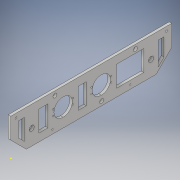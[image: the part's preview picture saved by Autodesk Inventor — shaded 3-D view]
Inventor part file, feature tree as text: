
AUTODESK INVENTOR PART (.ipt)
format: ipt  version: 2017 (Build 210142000, 142)  size: 301,568 bytes
history: native  units: in
note: dims shown in document units (in); Inventor stores cm internally (conversion verified against a paired STEP export)
features: sketch x15, hole x8, extrude x7, chamfer x3, thicken_offset x1, projected_geometry x1
ambient origin geometry x8: Origin, YZ Plane, XZ Plane, XY Plane, X Axis, Y Axis, Z Axis, Center Point
bodies: Solid1 (feature_tree)
feature tree (35):
  extrude  "Extrusion1"  Depth=15.5in
  sketch  "Sketch3"  dims[d4=2.0in]
  sketch  "Sketch4"  dims[d5=1.0in]
  chamfer  "Chamfer1"  Distance=0.25in
  chamfer  "Chamfer2"  Distance=1.5in Angle=45.0deg
  hole  "Hole1"  [1 undecoded]
  hole  "Hole3"  [1 undecoded]
  sketch  "Sketch8"  dims[d13=1.5in d14=0.125in d15=45.0deg d16=2.0in]
  hole  "Hole4"  [1 undecoded]
  hole  "Hole6"  [1 undecoded]
  extrude  "Extrusion2"  Depth=0.5in
  thicken_offset  "Thicken1"
  sketch  "Sketch16"  dims[d20=0.501in d21=0.75in d22=0.375in d23=0.25in d24=0.5635in d25=1.0in d26=0.8108in d42=0.394in]
  sketch  "Sketch17"  dims[d43=3.75in d44=3.75in]
  sketch  "Sketch18"  dims[d45=0.144in d46=0.5in]
  hole  "Hole10"  [1 undecoded]
  hole  "Hole11"  [1 undecoded]
  hole  "Hole12"  [1 undecoded]
  hole  "Hole13"  [1 undecoded]
  sketch  "Sketch19"  dims[d47=0.5in]
  sketch  "Sketch20"  dims[d48=0.188in d49=0.75in d50=0.375in d51=0.25in d52=0.5635in d53=1.0in d54=0.8108in d57=0.394in]
  extrude  "Extrusion3"  Depth=0.75in
  extrude  "Extrusion4"  Depth=0.75in
  sketch  "Sketch21"  dims[d61=0.14in d62=0.75in d63=0.375in d64=0.25in d65=0.5635in d66=1.0in d67=0.8108in]
  extrude  "Extrusion5"  Depth=0.75in
  extrude  "Extrusion6"  Depth=0.75in
  extrude  "Extrusion7"  Depth=0.75in
  chamfer  "Chamfer5"  Distance=0.945in
  sketch  "Sketch1"  dims[d2=3.25in d3=15.5in]
  sketch  "Sketch5"  dims[d6=2.0in]
  projected_geometry  "Projected Loop1"
  sketch  "Sketch7"  dims[d7=1.0in d8=0.25in d9=0.0in d10=1.5in d11=0.125in d12=45.0deg]
  sketch  "Sketch10"  dims[d17=1.5in d18=1.5in]
  sketch  "Sketch14"  dims[d19=2.0in]
  sketch  "Sketch22"  dims[d75=1.7in d76=0.75in d77=0.375in d78=0.25in d79=0.5635in d80=1.0in d81=0.8108in d82=0.144in d108=1.5in d109=1.5in d113=0.945in d114=0.276in d115=0.276in d116=0.945in d117=0.945in d118=0.945in d119=0.138in d120=0.138in d121=0.138in d122=0.138in d123=0.138in d124=1.0in d125=0.0in d128=8.75in d129=0.25in d130=0.25in d131=0.4in d132=0.4in d133=3.0in d135=0.14in d136=3.5in d138=0.14in d139=0.394in d141=4.0in d143=4.0in d145=0.188in d146=0.188in d147=0.14in d148=0.75in d149=0.375in d150=0.25in d151=0.5635in d152=1.0in d153=0.8108in d154=0.14in d155=0.75in d156=0.375in d157=0.25in d158=0.5635in d159=1.0in d160=0.8108in d161=0.14in d162=0.75in d163=0.375in d164=0.25in d165=0.5635in d166=1.0in d167=0.8108in d168=0.14in d169=0.75in d170=0.375in d171=0.25in d172=0.5635in d173=1.0in d174=0.8108in d183=0.75in d184=0.75in d185=0.75in d186=0.45in d187=0.45in d188=0.45in d189=0.45in d190=0.75in d191=1.0in d192=0.0in d193=1.0in d194=0.0in d195=0.75in d196=0.45in d197=0.45in d198=0.75in d199=0.75in d200=0.75in d201=0.45in d202=0.45in d203=1.0in d204=0.0in d205=1.0in d206=0.0in d207=0.75in d208=0.45in d209=0.75in d210=1.0in d211=0.0in d212=0.125in d213=0.125in d214=45.0deg d177=1.0in d178=1.0in]
note: 8 required parameter values undecoded (feature->parameter linkage not recoverable at this tier; creation-order binding heuristic only, values carry confidence <= 0.55)
